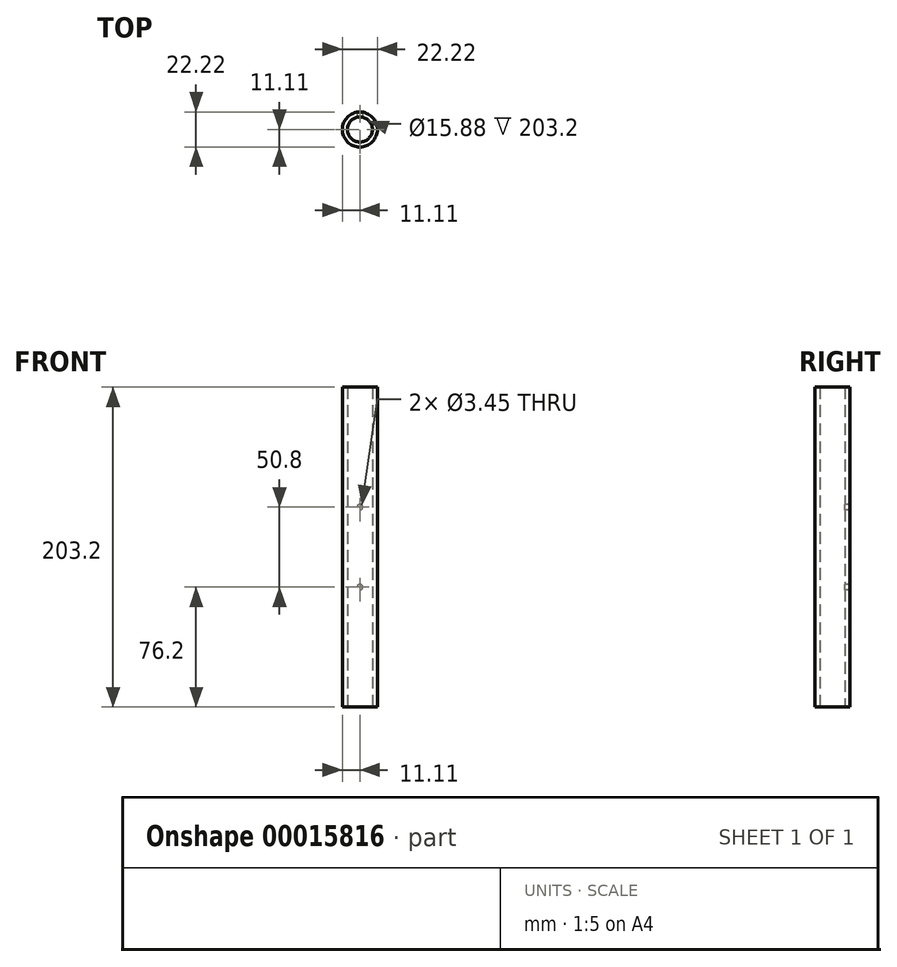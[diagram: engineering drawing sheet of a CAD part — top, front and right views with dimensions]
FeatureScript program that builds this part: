
annotation { "Feature Type Name" : "Feature", "Feature Type Description" : "" }
export const myFeature = defineFeature(function(context is Context, id is Id, definition is map)
    precondition{}
    {
        {
            var Q0;
            Q0=qCreatedBy(makeId("Top.planeOp"),FACE);
            var sketch = newSketch(context, id + "F0", { "sketchPlane" : qUnion([Q0])});
            skCircle(sketch, "E0", {"center": v(0, 0) * mm, "radius": 7.94 * mm});
            skCircle(sketch, "E1", {"center": v(0, 0) * mm, "radius": 11.11 * mm});
            skSolve(sketch);
        }
        {
            var Q0;
            Q0=qSketchRegion(id+"F0",true);
            extrude(context, id + "F1", {"entities" : qUnion([Q0]), "depth" : 203.2 * mm});
        }
        {
            var Q0;
            Q0=qCreatedBy(makeId("Front.planeOp"),FACE);
            var sketch = newSketch(context, id + "F2", { "sketchPlane" : qUnion([Q0])});
            skLineSegment(sketch, "E2", {"start": v(0, 203.2) * mm, "end": v(0, 127) * mm, "construction": true});
            skLineSegment(sketch, "E3", {"start": v(0, 127) * mm, "end": v(0, 76.2) * mm, "construction": true});
            skLineSegment(sketch, "E4", {"start": v(0, 76.2) * mm, "end": v(0, 0) * mm, "construction": true});
            skCircle(sketch, "E5", {"center": v(0, 127) * mm, "radius": 1.73 * mm});
            skCircle(sketch, "E6", {"center": v(0, 76.2) * mm, "radius": 1.73 * mm});
            skSolve(sketch);
        }
        {
            var Q0;
            Q0=qSketchRegion(id+"F2",true);
            var Q1;
            Q1=makeQuery(id+"F1.opExtrude","SWEPT_FACE",FACE,{"disambiguationData":[OSD([sQuery(id+"F0.wireOp",EDGE,"E1")])]});
            extrude(context, id + "F3", {"entities" : qUnion([Q0]), "operationType" : NewBodyOperationType.REMOVE, "endBound" : BoundingType.UP_TO_SURFACE, "oppositeDirection" : true, "endBoundEntityFace" : qUnion([Q1]), "depth" : 25.4 * mm});
        }
    });
